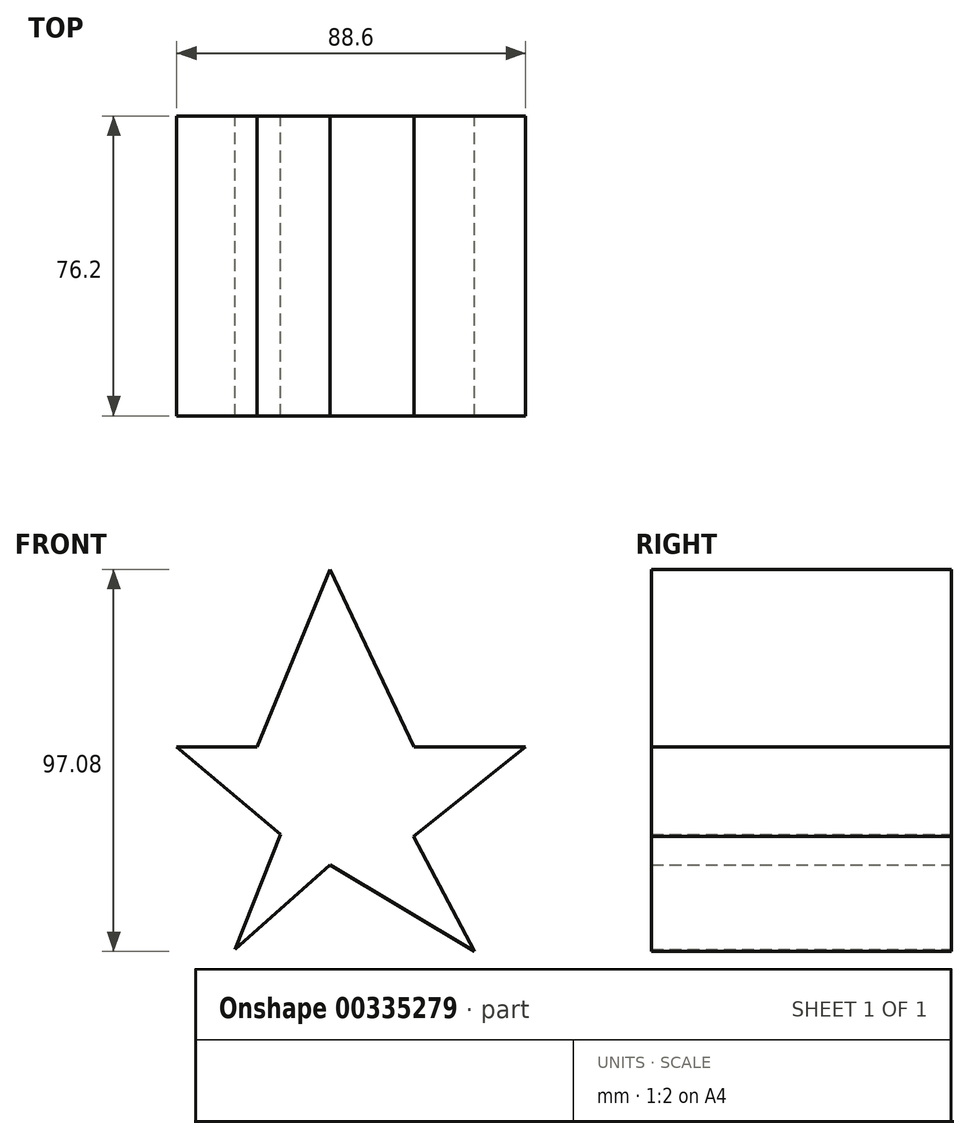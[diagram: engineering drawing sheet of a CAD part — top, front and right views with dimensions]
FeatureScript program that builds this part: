
annotation { "Feature Type Name" : "Feature", "Feature Type Description" : "" }
export const myFeature = defineFeature(function(context is Context, id is Id, definition is map)
    precondition{}
    {
        {
            var Q0;
            Q0=qCreatedBy(makeId("Front.planeOp"),FACE);
            var sketch = newSketch(context, id + "F0", { "sketchPlane" : qUnion([Q0])});
            skLineSegment(sketch, "E0", {"start": v(0, 45.11) * mm, "end": v(21.3, 0) * mm});
            skLineSegment(sketch, "E1", {"start": v(21.3, 0) * mm, "end": v(49.62, 0) * mm});
            skLineSegment(sketch, "E2", {"start": v(49.62, 0) * mm, "end": v(21.11, -22.74) * mm});
            skLineSegment(sketch, "E3", {"start": v(21.11, -22.74) * mm, "end": v(36.63, -51.97) * mm});
            skLineSegment(sketch, "E4", {"start": v(36.63, -51.97) * mm, "end": v(0, -29.95) * mm});
            skLineSegment(sketch, "E5", {"start": v(0, -29.95) * mm, "end": v(-24.18, -51.43) * mm});
            skLineSegment(sketch, "E6", {"start": v(-24.18, -51.43) * mm, "end": v(-12.63, -22.2) * mm});
            skLineSegment(sketch, "E7", {"start": v(-12.63, -22.2) * mm, "end": v(-38.98, 0) * mm});
            skLineSegment(sketch, "E8", {"start": v(-38.98, 0) * mm, "end": v(-18.59, 0) * mm});
            skLineSegment(sketch, "E9", {"start": v(-18.59, 0) * mm, "end": v(0, 45.11) * mm});
            skSolve(sketch);
        }
        {
            var Q0;
            Q0 = qSketchRegion(id + "F0", true);
            extrude(context, id + "F1", {"entities" : qUnion([Q0]), "depth" : 76.2 * mm});
        }
    });
